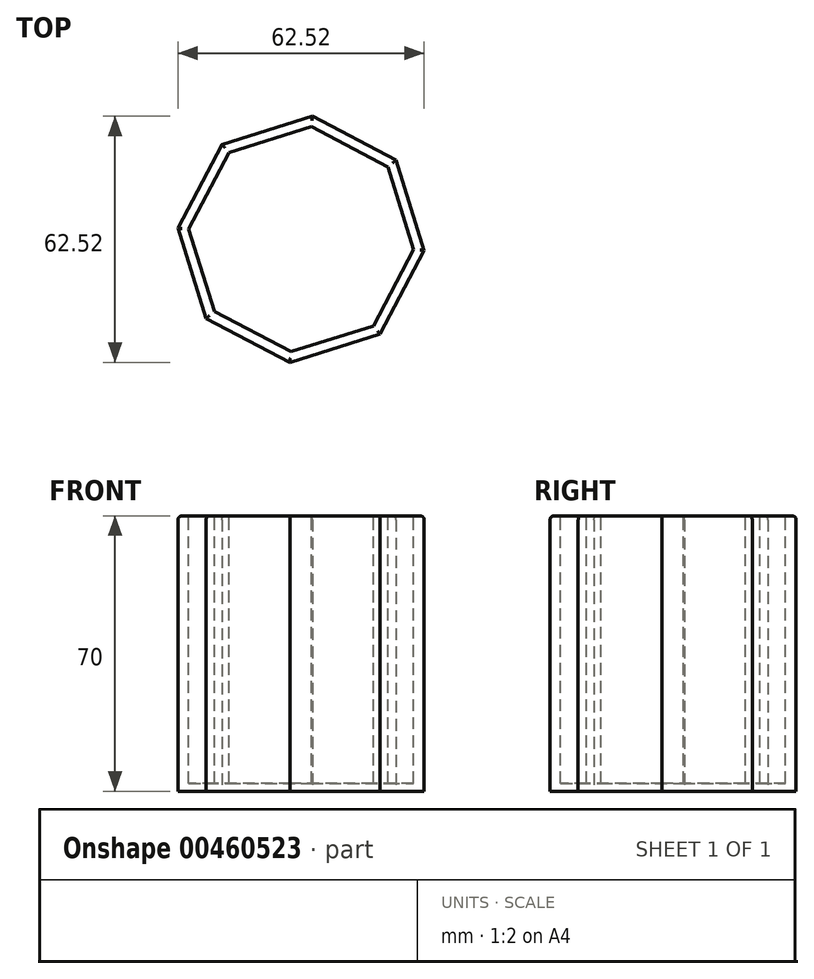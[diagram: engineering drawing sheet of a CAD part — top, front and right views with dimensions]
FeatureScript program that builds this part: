
annotation { "Feature Type Name" : "Feature", "Feature Type Description" : "" }
export const myFeature = defineFeature(function(context is Context, id is Id, definition is map)
    precondition{}
    {
        {
            var Q0;
            Q0=qCreatedBy(makeId("Top.planeOp"),FACE);
            var sketch = newSketch(context, id + "F0", { "sketchPlane" : qUnion([Q0])});
            skCircle(sketch, "E0.cCircle", {"center": v(0, 0) * mm, "radius": 29 * mm, "construction": true});
            skLineSegment(sketch, "E0.0", {"start": v(31.26, -2.84) * mm, "end": v(20.1, -24.12) * mm});
            skLineSegment(sketch, "E0.1", {"start": v(20.1, -24.12) * mm, "end": v(-2.84, -31.26) * mm});
            skLineSegment(sketch, "E0.2", {"start": v(-2.84, -31.26) * mm, "end": v(-24.12, -20.1) * mm});
            skLineSegment(sketch, "E0.3", {"start": v(-24.12, -20.1) * mm, "end": v(-31.26, 2.84) * mm});
            skLineSegment(sketch, "E0.4", {"start": v(-31.26, 2.84) * mm, "end": v(-20.1, 24.12) * mm});
            skLineSegment(sketch, "E0.5", {"start": v(-20.1, 24.12) * mm, "end": v(2.84, 31.26) * mm});
            skLineSegment(sketch, "E0.6", {"start": v(2.84, 31.26) * mm, "end": v(24.12, 20.1) * mm});
            skLineSegment(sketch, "E0.7", {"start": v(24.12, 20.1) * mm, "end": v(31.26, -2.84) * mm});
            skPoint(sketch, "E0.0.midPoint", {"position": v(25.68, -13.48) * mm});
            skSolve(sketch);
        }
        {
            var Q0;
            Q0 = qSketchRegion(id + "F0", true);
            extrude(context, id + "F1", {"entities" : qUnion([Q0]), "depth" : 70 * mm});
        }
        {
            var Q0;
            Q0=makeQuery(id+"F1.opExtrude","CAP_FACE",FACE,{"disambiguationData":[OSD([sQuery(id+"F0.wireOp",EDGE,"E0.0"),sQuery(id+"F0.wireOp",EDGE,"E0.1"),sQuery(id+"F0.wireOp",EDGE,"E0.2"),sQuery(id+"F0.wireOp",EDGE,"E0.3"),sQuery(id+"F0.wireOp",EDGE,"E0.4"),sQuery(id+"F0.wireOp",EDGE,"E0.5"),sQuery(id+"F0.wireOp",EDGE,"E0.6"),sQuery(id+"F0.wireOp",EDGE,"E0.7")])],"isStart":false});
            var sketch = newSketch(context, id + "F2", { "sketchPlane" : qUnion([Q0])});
            skCircle(sketch, "E1.cCircle", {"center": v(0, 0) * mm, "radius": 26.5 * mm, "construction": true});
            skLineSegment(sketch, "E1.0", {"start": v(28.57, -2.6) * mm, "end": v(18.36, -22.04) * mm});
            skLineSegment(sketch, "E1.1", {"start": v(18.36, -22.04) * mm, "end": v(-2.6, -28.57) * mm});
            skLineSegment(sketch, "E1.2", {"start": v(-2.6, -28.57) * mm, "end": v(-22.04, -18.36) * mm});
            skLineSegment(sketch, "E1.3", {"start": v(-22.04, -18.36) * mm, "end": v(-28.57, 2.6) * mm});
            skLineSegment(sketch, "E1.4", {"start": v(-28.57, 2.6) * mm, "end": v(-18.36, 22.04) * mm});
            skLineSegment(sketch, "E1.5", {"start": v(-18.36, 22.04) * mm, "end": v(2.6, 28.57) * mm});
            skLineSegment(sketch, "E1.6", {"start": v(2.6, 28.57) * mm, "end": v(22.04, 18.36) * mm});
            skLineSegment(sketch, "E1.7", {"start": v(22.04, 18.36) * mm, "end": v(28.57, -2.6) * mm});
            skPoint(sketch, "E1.0.midPoint", {"position": v(23.46, -12.32) * mm});
            skSolve(sketch);
        }
        {
            var Q0;
            Q0 = qSketchRegion(id + "F2", true);
            extrude(context, id + "F3", {"entities" : qUnion([Q0]), "operationType" : NewBodyOperationType.REMOVE, "oppositeDirection" : true, "depth" : 68 * mm});
        }
        {
            var Q0;
            Q0=makeQuery(id+"F1.opExtrude","CAP_EDGE",EDGE,{"disambiguationData":[OSD([sQuery(id+"F0.wireOp",EDGE,"E0.0")])],"isStart":false});
            var Q1;
            Q1=makeQuery(id+"F1.opExtrude","CAP_EDGE",EDGE,{"disambiguationData":[OSD([sQuery(id+"F0.wireOp",EDGE,"E0.7")])],"isStart":false});
            var Q2;
            Q2=makeQuery(id+"F1.opExtrude","CAP_EDGE",EDGE,{"disambiguationData":[OSD([sQuery(id+"F0.wireOp",EDGE,"E0.6")])],"isStart":false});
            var Q3;
            Q3=makeQuery(id+"F1.opExtrude","CAP_EDGE",EDGE,{"disambiguationData":[OSD([sQuery(id+"F0.wireOp",EDGE,"E0.5")])],"isStart":false});
            var Q4;
            Q4=makeQuery(id+"F1.opExtrude","CAP_EDGE",EDGE,{"disambiguationData":[OSD([sQuery(id+"F0.wireOp",EDGE,"E0.4")])],"isStart":false});
            var Q5;
            Q5=makeQuery(id+"F1.opExtrude","CAP_EDGE",EDGE,{"disambiguationData":[OSD([sQuery(id+"F0.wireOp",EDGE,"E0.3")])],"isStart":false});
            var Q6;
            Q6=makeQuery(id+"F1.opExtrude","CAP_EDGE",EDGE,{"disambiguationData":[OSD([sQuery(id+"F0.wireOp",EDGE,"E0.2")])],"isStart":false});
            var Q7;
            Q7=makeQuery(id+"F1.opExtrude","CAP_EDGE",EDGE,{"disambiguationData":[OSD([sQuery(id+"F0.wireOp",EDGE,"E0.1")])],"isStart":false});
            fillet(context, id + "F4", {"entities" : qUnion([Q0, Q1, Q2, Q3, Q4, Q5, Q6, Q7]), "radius" : 1 * mm, "tangentPropagation" : true, "allowEdgeOverflow" : false});
        }
    });
